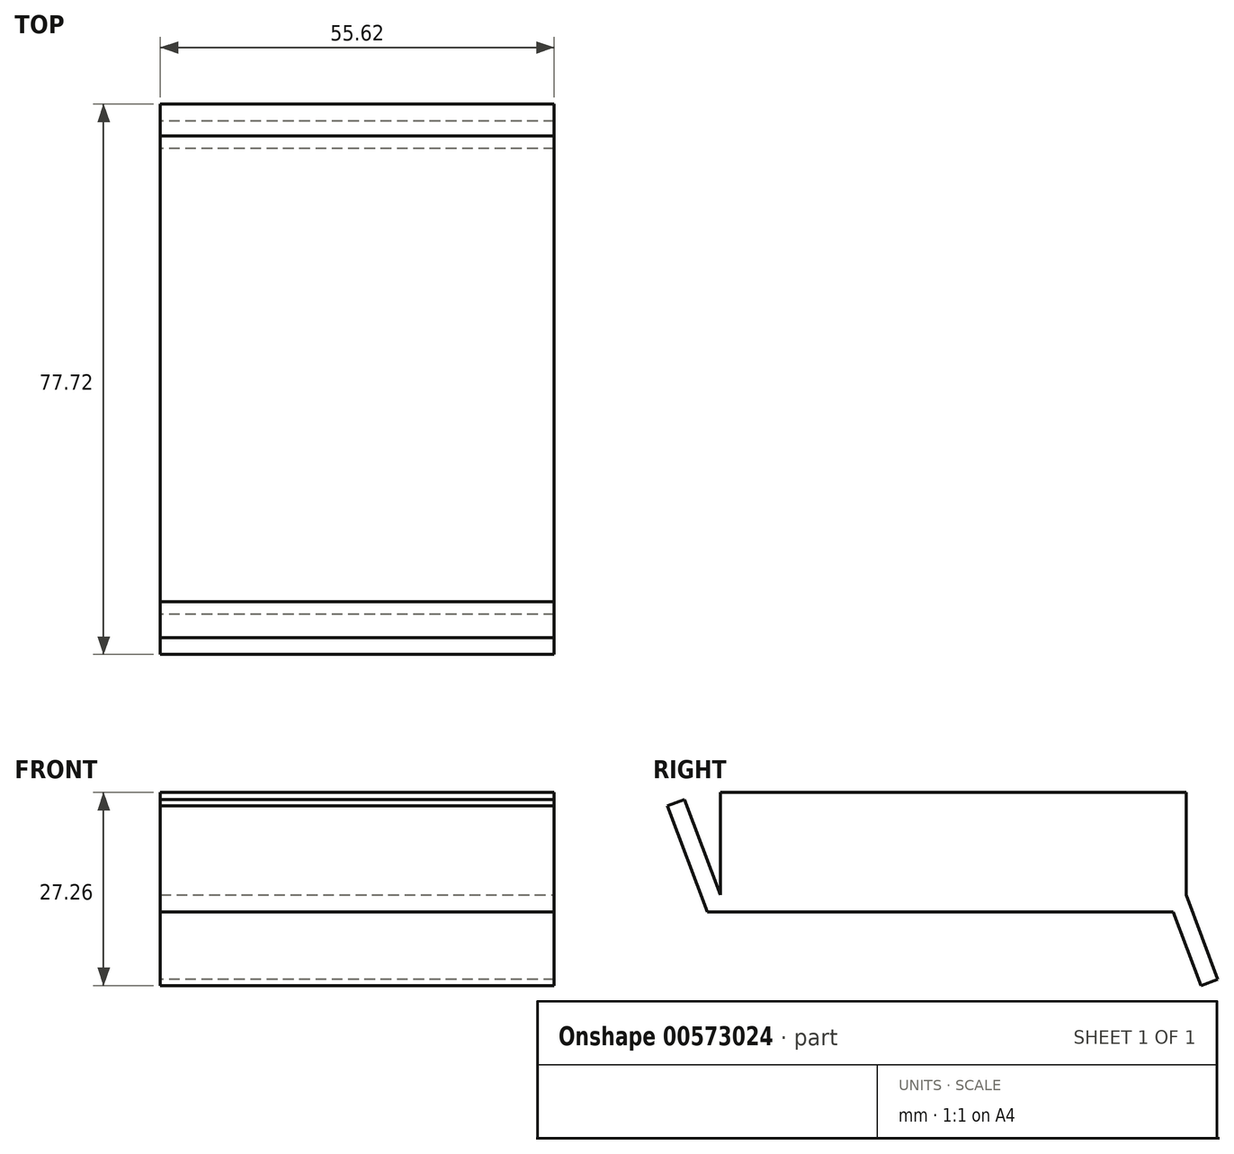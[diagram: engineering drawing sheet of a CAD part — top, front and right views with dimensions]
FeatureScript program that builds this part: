
annotation { "Feature Type Name" : "Feature", "Feature Type Description" : "" }
export const myFeature = defineFeature(function(context is Context, id is Id, definition is map)
    precondition{}
    {
        {
            var Q0;
            Q0=qCreatedBy(makeId("Top.planeOp"),FACE);
            var sketch = newSketch(context, id + "F0", { "sketchPlane" : qUnion([Q0])});
            skLineSegment(sketch, "E0.bottom", {"start": v(-27.81, 27.81) * mm, "end": v(27.81, 27.81) * mm});
            skLineSegment(sketch, "E0.top", {"start": v(-27.81, -27.81) * mm, "end": v(27.81, -27.81) * mm});
            skLineSegment(sketch, "E0.left", {"start": v(-27.81, 27.81) * mm, "end": v(-27.81, -27.81) * mm});
            skLineSegment(sketch, "E0.right", {"start": v(27.81, 27.81) * mm, "end": v(27.81, -27.81) * mm});
            skPoint(sketch, "E0.middle", {"position": v(0, 0) * mm});
            skSolve(sketch);
        }
        {
            var Q0;
            Q0 = qSketchRegion(id + "F0", true);
            extrude(context, id + "F1", {"entities" : qUnion([Q0]), "depth" : 14.48 * mm, "offsetDistance" : 25.4 * mm});
        }
        {
            var Q0;
            Q0=makeQuery(id+"F1.opExtrude","SWEPT_FACE",FACE,{"disambiguationData":[OSD([sQuery(id+"F0.wireOp",EDGE,"E0.top")])]});
            var sketch = newSketch(context, id + "F2", { "sketchPlane" : qUnion([Q0])});
            skLineSegment(sketch, "E1.bottom", {"start": v(-27.81, 14.48) * mm, "end": v(27.81, 14.48) * mm});
            skLineSegment(sketch, "E1.top", {"start": v(-27.81, 0) * mm, "end": v(27.81, 0) * mm});
            skLineSegment(sketch, "E1.left", {"start": v(-27.81, 14.48) * mm, "end": v(-27.81, 0) * mm});
            skLineSegment(sketch, "E1.right", {"start": v(27.81, 14.48) * mm, "end": v(27.81, 0) * mm});
            skSolve(sketch);
        }
        {
            var Q0;
            Q0 = qSketchRegion(id + "F2", true);
            extrude(context, id + "F3", {"entities" : qUnion([Q0]), "operationType" : NewBodyOperationType.ADD, "depth" : 10.16 * mm, "offsetDistance" : 25.4 * mm});
        }
        {
            var Q0;
            Q0=makeQuery(id+"F3.boolean.opBoolean","MERGE",FACE,{"derivedFrom":[makeQuery(id+"F1.opExtrude","SWEPT_FACE",FACE,{"disambiguationData":[OSD([sQuery(id+"F0.wireOp",EDGE,"E0.left")])]}),makeQuery(id+"F3.opExtrude","SWEPT_FACE",FACE,{"disambiguationData":[OSD([sQuery(id+"F2.wireOp",EDGE,"E1.left")])]})]});
            var sketch = newSketch(context, id + "F4", { "sketchPlane" : qUnion([Q0])});
            skLineSegment(sketch, "E2.0", {"start": v(-27.81, 0) * mm, "end": v(37.97, 0) * mm});
            skLineSegment(sketch, "E3", {"start": v(-27.81, 0) * mm, "end": v(-32.29, -11.89) * mm});
            skLineSegment(sketch, "E4", {"start": v(37.97, 0) * mm, "end": v(43.05, 13.49) * mm});
            skLineSegment(sketch, "E5", {"start": v(43.05, 13.49) * mm, "end": v(45.43, 12.6) * mm});
            skLineSegment(sketch, "E6", {"start": v(45.43, 12.6) * mm, "end": v(40.69, 0) * mm});
            skLineSegment(sketch, "E7", {"start": v(40.69, 0) * mm, "end": v(39.8, -2.38) * mm});
            skLineSegment(sketch, "E8", {"start": v(39.8, -2.38) * mm, "end": v(-26, -2.38) * mm});
            skLineSegment(sketch, "E9", {"start": v(-32.29, -11.89) * mm, "end": v(-29.91, -12.78) * mm});
            skLineSegment(sketch, "E10", {"start": v(-29.91, -12.78) * mm, "end": v(-26, -2.38) * mm});
            skSolve(sketch);
        }
        {
            var Q0;
            Q0 = qSketchRegion(id + "F4", true);
            extrude(context, id + "F5", {"entities" : qUnion([Q0]), "operationType" : NewBodyOperationType.ADD, "oppositeDirection" : true, "depth" : 55.63 * mm, "offsetDistance" : 25.4 * mm});
        }
    });
